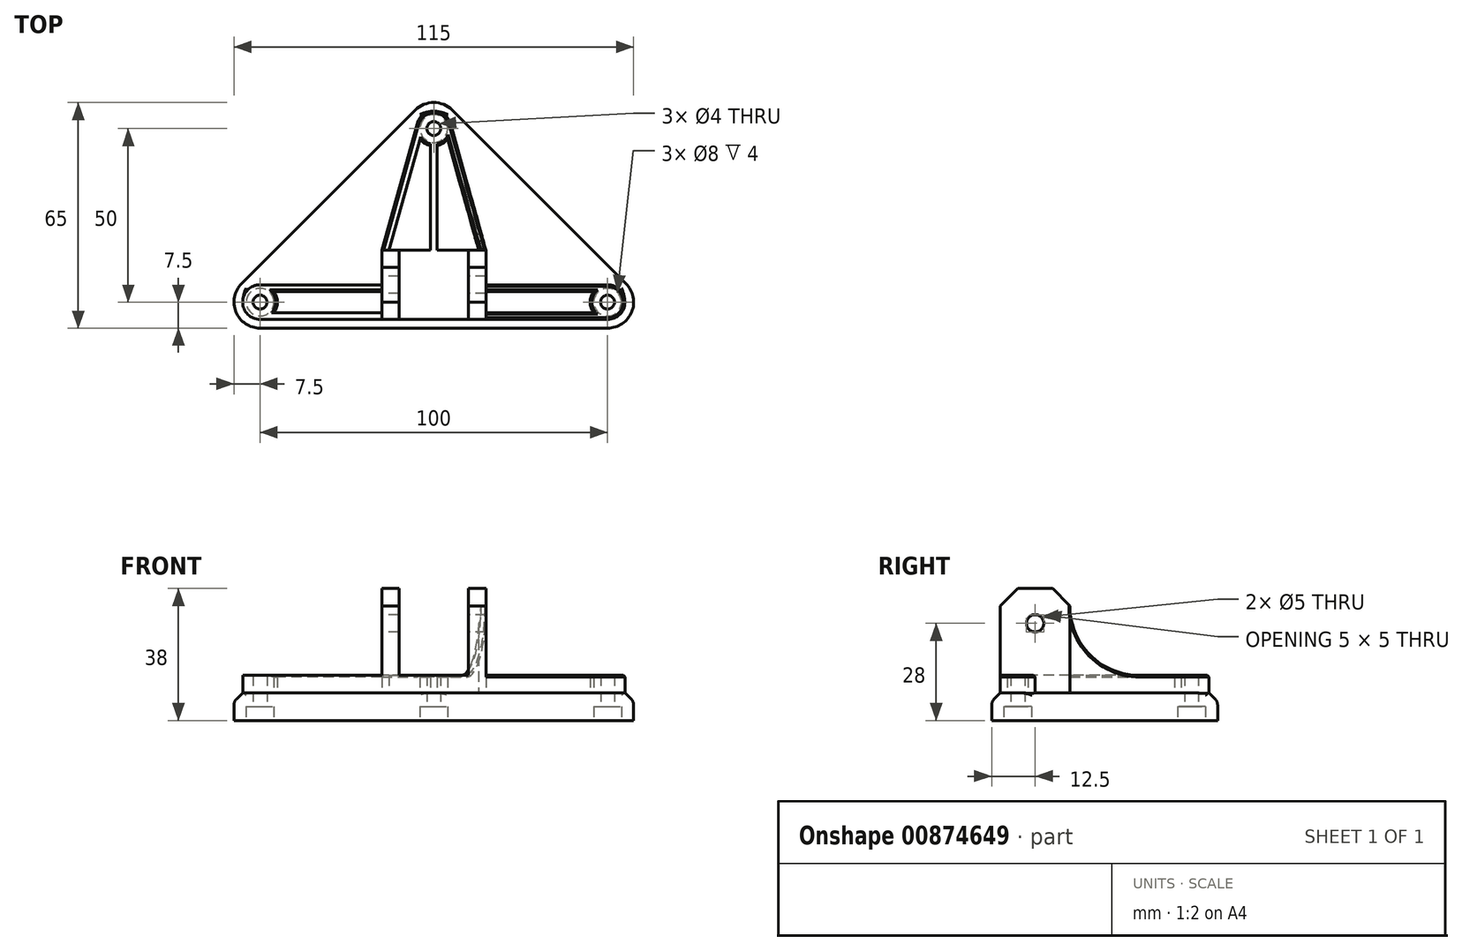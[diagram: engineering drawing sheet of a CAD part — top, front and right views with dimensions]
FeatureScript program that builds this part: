
annotation { "Feature Type Name" : "Feature", "Feature Type Description" : "" }
export const myFeature = defineFeature(function(context is Context, id is Id, definition is map)
    precondition{}
    {
        {
            var Q0;
            Q0=qCreatedBy(makeId("Top.planeOp"),FACE);
            var sketch = newSketch(context, id + "F0", { "sketchPlane" : qUnion([Q0])});
            skCircle(sketch, "E0", {"center": v(-50, 0) * mm, "radius": 2 * mm});
            skLineSegment(sketch, "E1", {"start": v(0, 0) * mm, "end": v(0, 50) * mm, "construction": true});
            skCircle(sketch, "E2", {"center": v(0, 50) * mm, "radius": 2 * mm});
            skCircle(sketch, "E3.MirrorC", {"center": v(50, 0) * mm, "radius": 2 * mm});
            skArc(sketch, "E4", {"start": v(-55.3, 5.3) * mm, "mid": v(-56.93, -2.87) * mm, "end": v(-50, -7.5) * mm});
            skArc(sketch, "E5", {"start": v(50, -7.5) * mm, "mid": v(56.93, -2.87) * mm, "end": v(55.3, 5.3) * mm});
            skArc(sketch, "E6", {"start": v(5.3, 55.3) * mm, "mid": v(0, 57.5) * mm, "end": v(-5.3, 55.3) * mm});
            skLineSegment(sketch, "E7", {"start": v(-50, -7.5) * mm, "end": v(50, -7.5) * mm});
            skLineSegment(sketch, "E8", {"start": v(5.3, 55.3) * mm, "end": v(55.3, 5.3) * mm});
            skLineSegment(sketch, "E9", {"start": v(-55.3, 5.3) * mm, "end": v(-5.3, 55.3) * mm});
            skSolve(sketch);
        }
        {
            var Q0;
            Q0 = qSketchRegion(id + "F0", true);
            extrude(context, id + "F1", {"entities" : qUnion([Q0]), "depth" : 8 * mm, "offsetDistance" : 25 * mm});
        }
        {
            var Q0;
            Q0=makeQuery(id+"F1.opExtrude","CAP_FACE",FACE,{"disambiguationData":[OSD([sQuery(id+"F0.wireOp",EDGE,"E0"),sQuery(id+"F0.wireOp",EDGE,"E2"),sQuery(id+"F0.wireOp",EDGE,"E3.MirrorC"),sQuery(id+"F0.wireOp",EDGE,"E4"),sQuery(id+"F0.wireOp",EDGE,"E5"),sQuery(id+"F0.wireOp",EDGE,"E6"),sQuery(id+"F0.wireOp",EDGE,"E7"),sQuery(id+"F0.wireOp",EDGE,"E8"),sQuery(id+"F0.wireOp",EDGE,"E9")])],"isStart":true});
            var sketch = newSketch(context, id + "F2", { "sketchPlane" : qUnion([Q0])});
            skCircle(sketch, "E10", {"center": v(-50, 0) * mm, "radius": 4 * mm});
            skCircle(sketch, "E11", {"center": v(0, -50) * mm, "radius": 4 * mm});
            skCircle(sketch, "E12", {"center": v(50, 0) * mm, "radius": 4 * mm});
            skSolve(sketch);
        }
        {
            var Q0;
            Q0 = qSketchRegion(id + "F2", true);
            extrude(context, id + "F3", {"entities" : qUnion([Q0]), "operationType" : NewBodyOperationType.REMOVE, "oppositeDirection" : true, "depth" : 4 * mm, "offsetDistance" : 25 * mm});
        }
        {
            var Q0;
            Q0=makeQuery(id+"F1.opExtrude","CAP_EDGE",EDGE,{"disambiguationData":[OSD([sQuery(id+"F0.wireOp",EDGE,"E8")])],"isStart":false});
            chamfer(context, id + "F4", {"entities" : qUnion([Q0]), "width" : 2.5 * mm, "tangentPropagation" : true});
        }
        {
            var Q0;
            Q0=makeQuery(id+"F1.opExtrude","CAP_FACE",FACE,{"disambiguationData":[OSD([sQuery(id+"F0.wireOp",EDGE,"E0"),sQuery(id+"F0.wireOp",EDGE,"E2"),sQuery(id+"F0.wireOp",EDGE,"E3.MirrorC"),sQuery(id+"F0.wireOp",EDGE,"E4"),sQuery(id+"F0.wireOp",EDGE,"E5"),sQuery(id+"F0.wireOp",EDGE,"E6"),sQuery(id+"F0.wireOp",EDGE,"E7"),sQuery(id+"F0.wireOp",EDGE,"E8"),sQuery(id+"F0.wireOp",EDGE,"E9")])],"isStart":false});
            var sketch = newSketch(context, id + "F5", { "sketchPlane" : qUnion([Q0])});
            skLineSegment(sketch, "E13.bottom", {"start": v(15, -5) * mm, "end": v(-15, -5) * mm});
            skLineSegment(sketch, "E13.top", {"start": v(15, 15) * mm, "end": v(-15, 15) * mm});
            skLineSegment(sketch, "E13.left", {"start": v(15, -5) * mm, "end": v(15, 15) * mm});
            skLineSegment(sketch, "E13.right", {"start": v(-15, -5) * mm, "end": v(-15, 15) * mm});
            skPoint(sketch, "E13.middle", {"position": v(0, 5) * mm});
            skCircle(sketch, "E14.0", {"center": v(50, 0) * mm, "radius": 2 * mm, "construction": true});
            skSolve(sketch);
        }
        {
            var Q0;
            Q0 = qSketchRegion(id + "F5", true);
            extrude(context, id + "F6", {"entities" : qUnion([Q0]), "operationType" : NewBodyOperationType.ADD, "depth" : 5 * mm, "offsetDistance" : 25 * mm});
        }
        {
            var Q0;
            Q0=makeQuery(id+"F6.opExtrude","CAP_FACE",FACE,{"disambiguationData":[OSD([sQuery(id+"F5.wireOp",EDGE,"E13.bottom"),sQuery(id+"F5.wireOp",EDGE,"E13.top"),sQuery(id+"F5.wireOp",EDGE,"E13.left"),sQuery(id+"F5.wireOp",EDGE,"E13.right")])],"isStart":false});
            var sketch = newSketch(context, id + "F7", { "sketchPlane" : qUnion([Q0])});
            skLineSegment(sketch, "E15.bottom", {"start": v(-15, 15) * mm, "end": v(-10, 15) * mm});
            skLineSegment(sketch, "E15.top", {"start": v(-15, -5) * mm, "end": v(-10, -5) * mm});
            skLineSegment(sketch, "E15.left", {"start": v(-15, 15) * mm, "end": v(-15, -5) * mm});
            skLineSegment(sketch, "E15.right", {"start": v(-10, 15) * mm, "end": v(-10, -5) * mm});
            skLineSegment(sketch, "E16.bottom", {"start": v(15, 15) * mm, "end": v(10, 15) * mm});
            skLineSegment(sketch, "E16.top", {"start": v(15, -5) * mm, "end": v(10, -5) * mm});
            skLineSegment(sketch, "E16.left", {"start": v(15, 15) * mm, "end": v(15, -5) * mm});
            skLineSegment(sketch, "E16.right", {"start": v(10, 15) * mm, "end": v(10, -5) * mm});
            skSolve(sketch);
        }
        {
            var Q0;
            Q0 = qSketchRegion(id + "F7", true);
            extrude(context, id + "F8", {"entities" : qUnion([Q0]), "operationType" : NewBodyOperationType.ADD, "depth" : 25 * mm, "offsetDistance" : 25 * mm});
        }
        {
            var Q0;
            Q0=makeQuery(id+"F8.opExtrude","CAP_EDGE",EDGE,{"disambiguationData":[OSD([sQuery(id+"F7.wireOp",EDGE,"E15.bottom")])],"isStart":false});
            var Q1;
            Q1=makeQuery(id+"F8.opExtrude","CAP_EDGE",EDGE,{"disambiguationData":[OSD([sQuery(id+"F7.wireOp",EDGE,"E15.top")])],"isStart":false});
            var Q2;
            Q2=makeQuery(id+"F8.opExtrude","CAP_EDGE",EDGE,{"disambiguationData":[OSD([sQuery(id+"F7.wireOp",EDGE,"E16.bottom")])],"isStart":false});
            var Q3;
            Q3=makeQuery(id+"F8.opExtrude","CAP_EDGE",EDGE,{"disambiguationData":[OSD([sQuery(id+"F7.wireOp",EDGE,"E16.top")])],"isStart":false});
            chamfer(context, id + "F9", {"entities" : qUnion([Q0, Q1, Q2, Q3]), "width" : 5 * mm, "tangentPropagation" : true});
        }
        {
            var Q0;
            Q0=makeQuery(id+"F1.opExtrude","CAP_FACE",FACE,{"disambiguationData":[OSD([sQuery(id+"F0.wireOp",EDGE,"E0"),sQuery(id+"F0.wireOp",EDGE,"E2"),sQuery(id+"F0.wireOp",EDGE,"E3.MirrorC"),sQuery(id+"F0.wireOp",EDGE,"E4"),sQuery(id+"F0.wireOp",EDGE,"E5"),sQuery(id+"F0.wireOp",EDGE,"E6"),sQuery(id+"F0.wireOp",EDGE,"E7"),sQuery(id+"F0.wireOp",EDGE,"E8"),sQuery(id+"F0.wireOp",EDGE,"E9")])],"isStart":false});
            var sketch = newSketch(context, id + "F10", { "sketchPlane" : qUnion([Q0])});
            skArc(sketch, "E17", {"start": v(-50, 5) * mm, "mid": v(-55, 0) * mm, "end": v(-50, -5) * mm});
            skArc(sketch, "E18", {"start": v(1, 45.1) * mm, "mid": v(0, 55) * mm, "end": v(-1, 45.1) * mm});
            skLineSegment(sketch, "E19.0", {"start": v(-50, -5) * mm, "end": v(-15, -5) * mm});
            skLineSegment(sketch, "E20", {"start": v(-50, 5) * mm, "end": v(-15, 5) * mm});
            skLineSegment(sketch, "E21", {"start": v(-15, 5) * mm, "end": v(-15, 3) * mm});
            skLineSegment(sketch, "E22", {"start": v(-15, 3) * mm, "end": v(-46, 3) * mm});
            skLineSegment(sketch, "E23", {"start": v(-15, -5) * mm, "end": v(-15, -3) * mm});
            skLineSegment(sketch, "E24", {"start": v(-15, -3) * mm, "end": v(-46, -3) * mm});
            skArc(sketch, "E25.trimOffspring", {"start": v(-46, -3) * mm, "mid": v(-45, 0) * mm, "end": v(-46, 3) * mm});
            skLineSegment(sketch, "E26", {"start": v(0, 0) * mm, "end": v(0, 15) * mm, "construction": true});
            skLineSegment(sketch, "E27.MirrorCS", {"start": v(15, -5) * mm, "end": v(15, -3) * mm});
            skLineSegment(sketch, "E28.MirrorCS", {"start": v(15, 5) * mm, "end": v(15, 3) * mm});
            skLineSegment(sketch, "E29.MirrorCS", {"start": v(50, -5) * mm, "end": v(15, -5) * mm});
            skLineSegment(sketch, "E30.MirrorCS", {"start": v(15, -3) * mm, "end": v(46, -3) * mm});
            skArc(sketch, "E31.MirrorCS", {"start": v(50, 5) * mm, "mid": v(55, 0) * mm, "end": v(50, -5) * mm});
            skLineSegment(sketch, "E32.MirrorCS", {"start": v(50, 5) * mm, "end": v(15, 5) * mm});
            skLineSegment(sketch, "E33.MirrorCS", {"start": v(15, 3) * mm, "end": v(46, 3) * mm});
            skArc(sketch, "E34.MirrorCS", {"start": v(46, -3) * mm, "mid": v(45, 0) * mm, "end": v(46, 3) * mm});
            skLineSegment(sketch, "E35", {"start": v(15, 15) * mm, "end": v(4.81, 51.35) * mm});
            skLineSegment(sketch, "E36", {"start": v(-15, 15) * mm, "end": v(-4.81, 51.35) * mm});
            skLineSegment(sketch, "E37", {"start": v(-15, 15) * mm, "end": v(-12.92, 15) * mm});
            skLineSegment(sketch, "E38", {"start": v(-12.92, 15) * mm, "end": v(-3.97, 46.96) * mm});
            skLineSegment(sketch, "E39", {"start": v(15, 15) * mm, "end": v(12.92, 15) * mm});
            skLineSegment(sketch, "E40", {"start": v(12.92, 15) * mm, "end": v(3.97, 46.96) * mm});
            skLineSegment(sketch, "E41.bottom", {"start": v(1, 15) * mm, "end": v(-1, 15) * mm});
            skLineSegment(sketch, "E41.left", {"start": v(1, 15) * mm, "end": v(1, 45.1) * mm});
            skLineSegment(sketch, "E41.right", {"start": v(-1, 15) * mm, "end": v(-1, 45.1) * mm});
            skPoint(sketch, "E41.middle", {"position": v(0, 30.05) * mm});
            skCircle(sketch, "E42.0", {"center": v(-50, 0) * mm, "radius": 2 * mm});
            skCircle(sketch, "E43.0", {"center": v(0, 50) * mm, "radius": 2 * mm});
            skCircle(sketch, "E44.0", {"center": v(50, 0) * mm, "radius": 2 * mm});
            skSolve(sketch);
        }
        {
            var Q0;
            Q0 = qSketchRegion(id + "F10", true);
            extrude(context, id + "F11", {"entities" : qUnion([Q0]), "operationType" : NewBodyOperationType.ADD, "depth" : 5 * mm, "offsetDistance" : 25 * mm});
        }
        {
            var Q0;
            Q0=makeQuery(id+"F11.opExtrude","CAP_EDGE",EDGE,{"disambiguationData":[OSD([sQuery(id+"F10.wireOp",EDGE,"E39")])],"isStart":false});
            var Q1;
            Q1=makeQuery(id+"F11.opExtrude","CAP_EDGE",EDGE,{"disambiguationData":[OSD([sQuery(id+"F10.wireOp",EDGE,"E37")])],"isStart":false});
            var Q2;
            Q2=makeQuery(id+"F11.opExtrude","CAP_EDGE",EDGE,{"disambiguationData":[OSD([sQuery(id+"F10.wireOp",EDGE,"E23")])],"isStart":false});
            var Q3;
            Q3=makeQuery(id+"F11.opExtrude","CAP_EDGE",EDGE,{"disambiguationData":[OSD([sQuery(id+"F10.wireOp",EDGE,"E27.MirrorCS")])],"isStart":false});
            fillet(context, id + "F12", {"entities" : qUnion([Q0, Q1, Q2, Q3]), "radius" : 20 * mm, "tangentPropagation" : true, "allowEdgeOverflow" : false});
        }
        {
            var Q0;
            Q0=makeQuery(id+"F11.opExtrude","CAP_EDGE",EDGE,{"disambiguationData":[OSD([sQuery(id+"F10.wireOp",EDGE,"E31.MirrorCS")])],"isStart":false});
            var Q1;
            {var subQ0=sQuery(id+"F10.wireOp",EDGE,"E18");var subQ1=sQuery(id+"F0.wireOp",EDGE,"E9");var subQ2=sQuery(id+"F0.wireOp",EDGE,"E8");var subQ3=makeQuery(id+"F1.opExtrude","CAP_FACE",FACE,{"disambiguationData":[OSD([sQuery(id+"F0.wireOp",EDGE,"E0"),sQuery(id+"F0.wireOp",EDGE,"E2"),sQuery(id+"F0.wireOp",EDGE,"E3.MirrorC"),sQuery(id+"F0.wireOp",EDGE,"E4"),sQuery(id+"F0.wireOp",EDGE,"E5"),sQuery(id+"F0.wireOp",EDGE,"E6"),sQuery(id+"F0.wireOp",EDGE,"E7"),subQ2,subQ1])],"isStart":false});var subQ5=makeQuery(id+"F10.imprint","INTERSECT",VERTEX,{"derivedFrom":[makeQuery(id+"F4.opChamfer","BLEND_EDGE",EDGE,{"blendedFrom":[makeQuery(id+"F1.opExtrude","CAP_EDGE",EDGE,{"disambiguationData":[OSD([subQ2])],"isStart":false}),subQ3],"blendedInto":[subQ3]}),subQ0]});Q1=makeQuery(id+"F11.opExtrude","CAP_EDGE",EDGE,{"disambiguationData":[OSD([subQ0]),TDD([makeQuery(id+"F10.imprint","IMPRINT",EDGE,{"disambiguationData":[TD([[subQ5,-1.0]])],"derivedFrom":subQ0}),makeQuery(id+"F10.imprint","IMPRINT",EDGE,{"disambiguationData":[TD([[makeQuery(id+"F10.imprint","INTERSECT",VERTEX,{"derivedFrom":[subQ0,sQuery(id+"F10.wireOp",EDGE,"E35")]}),-1.0]])],"derivedFrom":subQ0}),makeQuery(id+"F10.imprint","IMPRINT",EDGE,{"disambiguationData":[TD([[makeQuery(id+"F10.imprint","INTERSECT",VERTEX,{"derivedFrom":[subQ0,sQuery(id+"F10.wireOp",EDGE,"E36")]}),1.0]])],"derivedFrom":subQ0})])],"isStart":false});}
            var Q2;
            Q2=makeQuery(id+"F12.opFillet","BLEND_EDGE",EDGE,{"blendedFrom":[makeQuery(id+"F11.opExtrude","CAP_EDGE",EDGE,{"disambiguationData":[OSD([sQuery(id+"F10.wireOp",EDGE,"E37")])],"isStart":false}),makeQuery(id+"F11.opExtrude","SWEPT_FACE",FACE,{"disambiguationData":[OSD([sQuery(id+"F10.wireOp",EDGE,"E38")])]})],"blendedInto":[makeQuery(id+"F11.opExtrude","SWEPT_FACE",FACE,{"disambiguationData":[OSD([sQuery(id+"F10.wireOp",EDGE,"E38")])]})]});
            var Q3;
            Q3=makeQuery(id+"F12.opFillet","BLEND_EDGE",EDGE,{"blendedFrom":[makeQuery(id+"F11.opExtrude","CAP_EDGE",EDGE,{"disambiguationData":[OSD([sQuery(id+"F10.wireOp",EDGE,"E23")])],"isStart":false}),makeQuery(id+"F11.boolean.opBoolean","MERGE",FACE,{"derivedFrom":[makeQuery(id+"F8.boolean.opBoolean","MERGE",FACE,{"derivedFrom":[makeQuery(id+"F6.opExtrude","SWEPT_FACE",FACE,{"disambiguationData":[OSD([sQuery(id+"F5.wireOp",EDGE,"E13.bottom")])]}),makeQuery(id+"F8.opExtrude","SWEPT_FACE",FACE,{"disambiguationData":[OSD([sQuery(id+"F7.wireOp",EDGE,"E15.top")])]}),makeQuery(id+"F8.opExtrude","SWEPT_FACE",FACE,{"disambiguationData":[OSD([sQuery(id+"F7.wireOp",EDGE,"E16.top")])]})]}),makeQuery(id+"F11.opExtrude","SWEPT_FACE",FACE,{"disambiguationData":[OSD([sQuery(id+"F10.wireOp",EDGE,"E19.0")])]}),makeQuery(id+"F11.opExtrude","SWEPT_FACE",FACE,{"disambiguationData":[OSD([sQuery(id+"F10.wireOp",EDGE,"E29.MirrorCS")])]})]})],"blendedInto":[makeQuery(id+"F11.boolean.opBoolean","MERGE",FACE,{"derivedFrom":[makeQuery(id+"F8.boolean.opBoolean","MERGE",FACE,{"derivedFrom":[makeQuery(id+"F6.opExtrude","SWEPT_FACE",FACE,{"disambiguationData":[OSD([sQuery(id+"F5.wireOp",EDGE,"E13.bottom")])]}),makeQuery(id+"F8.opExtrude","SWEPT_FACE",FACE,{"disambiguationData":[OSD([sQuery(id+"F7.wireOp",EDGE,"E15.top")])]}),makeQuery(id+"F8.opExtrude","SWEPT_FACE",FACE,{"disambiguationData":[OSD([sQuery(id+"F7.wireOp",EDGE,"E16.top")])]})]}),makeQuery(id+"F11.opExtrude","SWEPT_FACE",FACE,{"disambiguationData":[OSD([sQuery(id+"F10.wireOp",EDGE,"E19.0")])]}),makeQuery(id+"F11.opExtrude","SWEPT_FACE",FACE,{"disambiguationData":[OSD([sQuery(id+"F10.wireOp",EDGE,"E29.MirrorCS")])]})]})]});
            var Q4;
            Q4=makeQuery(id+"F12.opFillet","BLEND_EDGE",EDGE,{"blendedFrom":[makeQuery(id+"F11.opExtrude","CAP_EDGE",EDGE,{"disambiguationData":[OSD([sQuery(id+"F10.wireOp",EDGE,"E23")])],"isStart":false}),makeQuery(id+"F11.opExtrude","SWEPT_FACE",FACE,{"disambiguationData":[OSD([sQuery(id+"F10.wireOp",EDGE,"E24")])]})],"blendedInto":[makeQuery(id+"F11.opExtrude","SWEPT_FACE",FACE,{"disambiguationData":[OSD([sQuery(id+"F10.wireOp",EDGE,"E24")])]})]});
            var Q5;
            Q5=makeQuery(id+"F11.opExtrude","CAP_EDGE",EDGE,{"disambiguationData":[OSD([sQuery(id+"F10.wireOp",EDGE,"E22")])],"isStart":false});
            var Q6;
            Q6=makeQuery(id+"F11.opExtrude","CAP_EDGE",EDGE,{"disambiguationData":[OSD([sQuery(id+"F10.wireOp",EDGE,"E25.trimOffspring")])],"isStart":false});
            var Q7;
            {var subQ0=sQuery(id+"F10.wireOp",EDGE,"E18");Q7=makeQuery(id+"F11.opExtrude","CAP_EDGE",EDGE,{"disambiguationData":[OSD([subQ0]),TDD([makeQuery(id+"F10.imprint","IMPRINT",EDGE,{"disambiguationData":[TD([[makeQuery(id+"F10.imprint","INTERSECT",VERTEX,{"derivedFrom":[subQ0,sQuery(id+"F10.wireOp",EDGE,"E41.left")]}),-1.0]])],"derivedFrom":subQ0})])],"isStart":false});}
            var Q8;
            {var subQ0=sQuery(id+"F10.wireOp",EDGE,"E18");Q8=makeQuery(id+"F11.opExtrude","CAP_EDGE",EDGE,{"disambiguationData":[OSD([subQ0]),TDD([makeQuery(id+"F10.imprint","IMPRINT",EDGE,{"disambiguationData":[TD([[makeQuery(id+"F10.imprint","INTERSECT",VERTEX,{"derivedFrom":[subQ0,sQuery(id+"F10.wireOp",EDGE,"E41.right")]}),1.0]])],"derivedFrom":subQ0})])],"isStart":false});}
            var Q9;
            Q9=makeQuery(id+"F12.opFillet","BLEND_EDGE",EDGE,{"blendedFrom":[makeQuery(id+"F11.opExtrude","CAP_EDGE",EDGE,{"disambiguationData":[OSD([sQuery(id+"F10.wireOp",EDGE,"E39")])],"isStart":false}),makeQuery(id+"F11.opExtrude","SWEPT_FACE",FACE,{"disambiguationData":[OSD([sQuery(id+"F10.wireOp",EDGE,"E40")])]})],"blendedInto":[makeQuery(id+"F11.opExtrude","SWEPT_FACE",FACE,{"disambiguationData":[OSD([sQuery(id+"F10.wireOp",EDGE,"E40")])]})]});
            var Q10;
            Q10=makeQuery(id+"F11.opExtrude","CAP_EDGE",EDGE,{"disambiguationData":[OSD([sQuery(id+"F10.wireOp",EDGE,"E33.MirrorCS")])],"isStart":false});
            var Q11;
            Q11=makeQuery(id+"F11.opExtrude","CAP_EDGE",EDGE,{"disambiguationData":[OSD([sQuery(id+"F10.wireOp",EDGE,"E34.MirrorCS")])],"isStart":false});
            var Q12;
            Q12=makeQuery(id+"F11.opExtrude","CAP_EDGE",EDGE,{"disambiguationData":[OSD([sQuery(id+"F10.wireOp",EDGE,"E30.MirrorCS")])],"isStart":false});
            chamfer(context, id + "F13", {"entities" : qUnion([Q0, Q1, Q2, Q3, Q4, Q5, Q6, Q7, Q8, Q9, Q10, Q11, Q12]), "width" : .5 * mm, "tangentPropagation" : true});
        }
        {
            var Q0;
            Q0=makeQuery(id+"F8.opExtrude","SWEPT_FACE",FACE,{"disambiguationData":[OSD([sQuery(id+"F7.wireOp",EDGE,"E16.right")])]});
            var sketch = newSketch(context, id + "F14", { "sketchPlane" : qUnion([Q0])});
            skCircle(sketch, "E45", {"center": v(-5, 28) * mm, "radius": 2.5 * mm});
            skPoint(sketch, "E45.centerSnap0", {"position": v(-5, 38) * mm});
            skSolve(sketch);
        }
        {
            var Q0;
            Q0 = qSketchRegion(id + "F14", true);
            extrude(context, id + "F15", {"entities" : qUnion([Q0]), "operationType" : NewBodyOperationType.REMOVE, "endBound" : BoundingType.THROUGH_ALL, "oppositeDirection" : true, "depth" : 25 * mm, "offsetDistance" : 25 * mm, "hasSecondDirection" : true, "secondDirectionBound" : SecondDirectionBoundingType.THROUGH_ALL, "secondDirectionOppositeDirection" : false, "secondDirectionDepth" : 25 * mm});
        }
        {
            var Q0;
            {var subQ0=sQuery(id+"F0.wireOp",EDGE,"E9");Q0=makeQuery(id+"F4.opChamfer","BLEND_EDGE",EDGE,{"blendedFrom":[makeQuery(id+"F1.opExtrude","CAP_EDGE",EDGE,{"disambiguationData":[OSD([subQ0])],"isStart":false}),makeQuery(id+"F1.opExtrude","CAP_FACE",FACE,{"disambiguationData":[OSD([sQuery(id+"F0.wireOp",EDGE,"E0"),sQuery(id+"F0.wireOp",EDGE,"E2"),sQuery(id+"F0.wireOp",EDGE,"E3.MirrorC"),sQuery(id+"F0.wireOp",EDGE,"E4"),sQuery(id+"F0.wireOp",EDGE,"E5"),sQuery(id+"F0.wireOp",EDGE,"E6"),sQuery(id+"F0.wireOp",EDGE,"E7"),sQuery(id+"F0.wireOp",EDGE,"E8"),subQ0])],"isStart":false})],"blendedInto":[makeQuery(id+"F1.opExtrude","CAP_FACE",FACE,{"disambiguationData":[OSD([sQuery(id+"F0.wireOp",EDGE,"E0"),sQuery(id+"F0.wireOp",EDGE,"E2"),sQuery(id+"F0.wireOp",EDGE,"E3.MirrorC"),sQuery(id+"F0.wireOp",EDGE,"E4"),sQuery(id+"F0.wireOp",EDGE,"E5"),sQuery(id+"F0.wireOp",EDGE,"E6"),sQuery(id+"F0.wireOp",EDGE,"E7"),sQuery(id+"F0.wireOp",EDGE,"E8"),subQ0])],"isStart":false})]});}
            var Q1;
            {var subQ0=sQuery(id+"F0.wireOp",EDGE,"E8");Q1=makeQuery(id+"F4.opChamfer","BLEND_EDGE",EDGE,{"blendedFrom":[makeQuery(id+"F1.opExtrude","CAP_EDGE",EDGE,{"disambiguationData":[OSD([subQ0])],"isStart":false}),makeQuery(id+"F1.opExtrude","CAP_FACE",FACE,{"disambiguationData":[OSD([sQuery(id+"F0.wireOp",EDGE,"E0"),sQuery(id+"F0.wireOp",EDGE,"E2"),sQuery(id+"F0.wireOp",EDGE,"E3.MirrorC"),sQuery(id+"F0.wireOp",EDGE,"E4"),sQuery(id+"F0.wireOp",EDGE,"E5"),sQuery(id+"F0.wireOp",EDGE,"E6"),sQuery(id+"F0.wireOp",EDGE,"E7"),subQ0,sQuery(id+"F0.wireOp",EDGE,"E9")])],"isStart":false})],"blendedInto":[makeQuery(id+"F1.opExtrude","CAP_FACE",FACE,{"disambiguationData":[OSD([sQuery(id+"F0.wireOp",EDGE,"E0"),sQuery(id+"F0.wireOp",EDGE,"E2"),sQuery(id+"F0.wireOp",EDGE,"E3.MirrorC"),sQuery(id+"F0.wireOp",EDGE,"E4"),sQuery(id+"F0.wireOp",EDGE,"E5"),sQuery(id+"F0.wireOp",EDGE,"E6"),sQuery(id+"F0.wireOp",EDGE,"E7"),subQ0,sQuery(id+"F0.wireOp",EDGE,"E9")])],"isStart":false})]});}
            var Q2;
            {var subQ0=sQuery(id+"F0.wireOp",EDGE,"E8");Q2=makeQuery(id+"F4.opChamfer","BLEND_EDGE",EDGE,{"blendedFrom":[makeQuery(id+"F1.opExtrude","CAP_EDGE",EDGE,{"disambiguationData":[OSD([subQ0])],"isStart":false}),makeQuery(id+"F1.opExtrude","SWEPT_FACE",FACE,{"disambiguationData":[OSD([subQ0])]})],"blendedInto":[makeQuery(id+"F1.opExtrude","SWEPT_FACE",FACE,{"disambiguationData":[OSD([subQ0])]})]});}
            fillet(context, id + "F16", {"entities" : qUnion([Q0, Q1, Q2]), "radius" : 2.5 * mm, "tangentPropagation" : true, "allowEdgeOverflow" : false});
        }
    });
